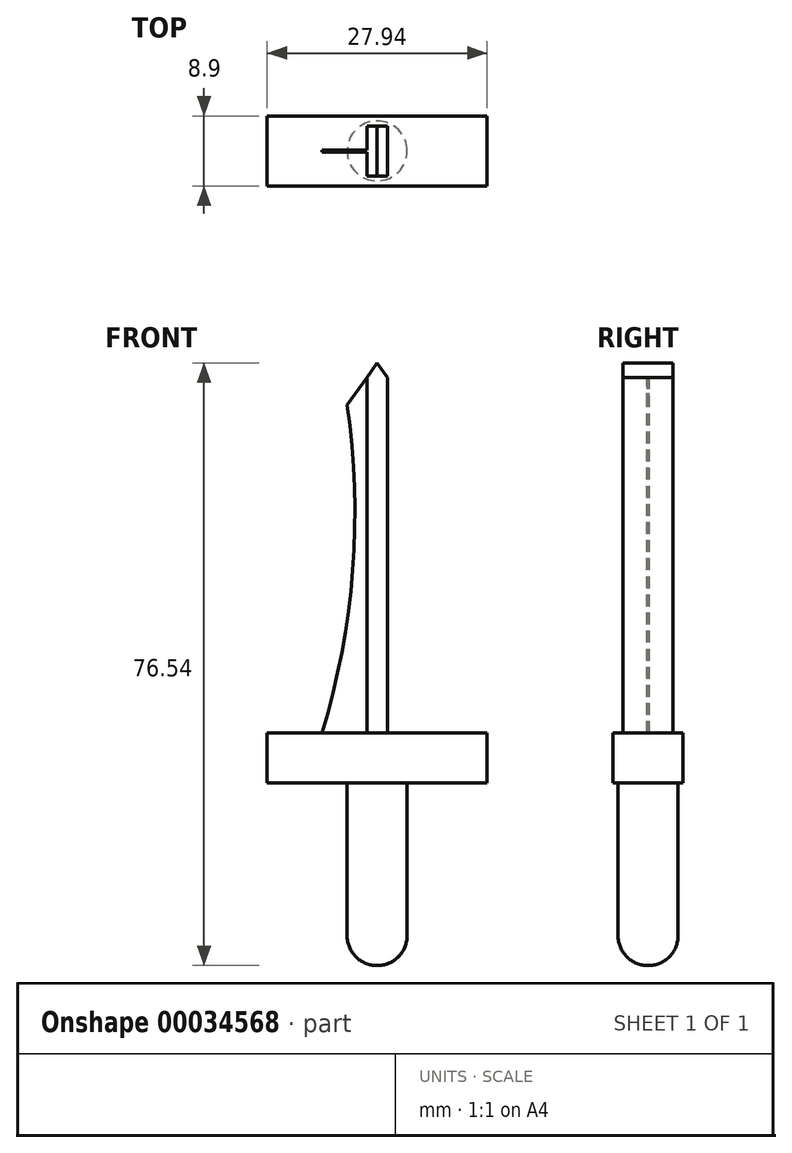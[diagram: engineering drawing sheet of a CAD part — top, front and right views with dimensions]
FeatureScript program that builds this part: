
annotation { "Feature Type Name" : "Feature", "Feature Type Description" : "" }
export const myFeature = defineFeature(function(context is Context, id is Id, definition is map)
    precondition{}
    {
        {
            var Q0;
            Q0=qCreatedBy(makeId("Front.planeOp"),FACE);
            var sketch = newSketch(context, id + "F0", { "sketchPlane" : qUnion([Q0])});
            skLineSegment(sketch, "E0.bottom", {"start": v(-34.27, 19.4) * mm, "end": v(-26.65, 19.4) * mm});
            skLineSegment(sketch, "E0.top", {"start": v(-34.27, 0.02) * mm, "end": v(-26.65, 0.02) * mm});
            skLineSegment(sketch, "E0.left", {"start": v(-34.27, 19.4) * mm, "end": v(-34.27, 0.02) * mm});
            skLineSegment(sketch, "E0.right", {"start": v(-26.65, 19.4) * mm, "end": v(-26.65, 0.02) * mm});
            skLineSegment(sketch, "E1.bottom", {"start": v(-44.43, 19.4) * mm, "end": v(-16.49, 19.4) * mm});
            skLineSegment(sketch, "E1.top", {"start": v(-44.43, 25.74) * mm, "end": v(-16.49, 25.74) * mm});
            skLineSegment(sketch, "E1.left", {"start": v(-44.43, 19.4) * mm, "end": v(-44.43, 25.74) * mm});
            skLineSegment(sketch, "E1.right", {"start": v(-16.49, 19.4) * mm, "end": v(-16.49, 25.74) * mm});
            skLineSegment(sketch, "E2", {"start": v(-34.27, 67.43) * mm, "end": v(-30.46, 72.73) * mm});
            skArc(sketch, "E3", {"start": v(-37.44, 25.74) * mm, "mid": v(-33.57, 46.41) * mm, "end": v(-34.27, 67.43) * mm});
            skLineSegment(sketch, "E4", {"start": v(-30.46, 72.73) * mm, "end": v(-30.46, 25.74) * mm});
            skArc(sketch, "E5.MirrorCS", {"start": v(-23.47, 25.74) * mm, "mid": v(-27.34, 46.41) * mm, "end": v(-26.65, 67.43) * mm});
            skLineSegment(sketch, "E6", {"start": v(-30.46, 72.73) * mm, "end": v(-26.65, 67.43) * mm});
            skPoint(sketch, "E7", {"position": v(-30.46, 19.4) * mm});
            skLineSegment(sketch, "E8", {"start": v(-30.46, 25.74) * mm, "end": v(-30.46, 19.4) * mm, "construction": true});
            skLineSegment(sketch, "E9", {"start": v(-30.46, 19.4) * mm, "end": v(-30.46, 0.02) * mm, "construction": true});
            skCircle(sketch, "E10", {"center": v(-30.46, 0) * mm, "radius": 3.81 * mm});
            skLineSegment(sketch, "E11", {"start": v(-26.65, 19.4) * mm, "end": v(-16.49, 19.4) * mm});
            skLineSegment(sketch, "E12", {"start": v(-34.27, 19.4) * mm, "end": v(-44.43, 19.4) * mm});
            skLineSegment(sketch, "E13", {"start": v(-44.43, 19.4) * mm, "end": v(-34.27, 19.4) * mm});
            skLineSegment(sketch, "E14", {"start": v(-30.46, 25.74) * mm, "end": v(-44.43, 25.74) * mm});
            skLineSegment(sketch, "E15", {"start": v(-30.46, 25.74) * mm, "end": v(-16.49, 25.74) * mm});
            skLineSegment(sketch, "E16", {"start": v(-30.46, 19.4) * mm, "end": v(-30.46, -3.81) * mm});
            skLineSegment(sketch, "E17", {"start": v(-31.76, 25.74) * mm, "end": v(-31.76, 70.92) * mm});
            skLineSegment(sketch, "E18", {"start": v(-29.15, 25.74) * mm, "end": v(-29.15, 70.92) * mm});
            skLineSegment(sketch, "E19", {"start": v(-30.46, 72.73) * mm, "end": v(-29.15, 70.92) * mm});
            skLineSegment(sketch, "E20", {"start": v(-30.46, 72.73) * mm, "end": v(-31.76, 70.92) * mm});
            skSolve(sketch);
        }
        {
            var Q0;
            {var subQ5=sQuery(id+"F0.wireOp",EDGE,"E0.right");Q0=makeQuery(id+"F0.imprint","IMPRINT",FACE,{"disambiguationData":[TD([[makeQuery(id+"F0.imprint","IMPRINT",EDGE,{"derivedFrom":subQ5}),-1.0]])]});}
            var Q1;
            {var subQ0=sQuery(id+"F0.wireOp",EDGE,"E16");var subQ3=sQuery(id+"F0.wireOp",EDGE,"E0.top");var subQ4=makeQuery(id+"F0.imprint","INTERSECT",VERTEX,{"derivedFrom":[subQ3,subQ0]});Q1=makeQuery(id+"F0.imprint","IMPRINT",FACE,{"disambiguationData":[TD([[makeQuery(id+"F0.imprint","IMPRINT",EDGE,{"disambiguationData":[TD([[subQ4,1.0]])],"derivedFrom":subQ0}),1.0]])]});}
            var Q2;
            {var subQ0=sQuery(id+"F0.wireOp",EDGE,"E16");var subQ3=sQuery(id+"F0.wireOp",EDGE,"E10");var subQ4=makeQuery(id+"F0.imprint","INTERSECT",VERTEX,{"disambiguationData":[OD(0.0)],"derivedFrom":[subQ3,subQ0]});Q2=makeQuery(id+"F0.imprint","IMPRINT",FACE,{"disambiguationData":[TD([[makeQuery(id+"F0.imprint","IMPRINT",EDGE,{"disambiguationData":[TD([[subQ4,1.0]])],"derivedFrom":subQ0}),1.0]])]});}
            var Q3;
            Q3=sQuery(id+"F0.wireOp",EDGE,"E9");
            revolve(context, id + "F1", {"entities" : qUnion([Q0, Q1, Q2]), "axis" : qUnion([Q3]), "revolveType" : RevolveType.FULL});
        }
        {
            var Q0;
            {var subQ6=sQuery(id+"F0.wireOp",EDGE,"E1.left");Q0=makeQuery(id+"F0.imprint","IMPRINT",FACE,{"disambiguationData":[TD([[makeQuery(id+"F0.imprint","IMPRINT",EDGE,{"derivedFrom":subQ6}),-1.0]])]});}
            extrude(context, id + "F2", {"entities" : qUnion([Q0]), "operationType" : NewBodyOperationType.ADD, "endBound" : BoundingType.SYMMETRIC, "depth" : 8.9 * mm});
        }
        {
            var Q0;
            {var subQ2=sQuery(id+"F0.wireOp",EDGE,"E5.MirrorCS");Q0=makeQuery(id+"F0.imprint","IMPRINT",FACE,{"disambiguationData":[TD([[makeQuery(id+"F0.imprint","IMPRINT",EDGE,{"derivedFrom":subQ2}),1.0]])]});}
            var Q1;
            Q1=makeQuery(id+"F0.imprint","IMPRINT",FACE,{"disambiguationData":[TD([[makeQuery(id+"F0.imprint","IMPRINT",EDGE,{"derivedFrom":sQuery(id+"F0.wireOp",EDGE,"E2")}),-1.0]])]});
            extrude(context, id + "F3", {"entities" : qUnion([Q0, Q1]), "operationType" : NewBodyOperationType.ADD, "endBound" : BoundingType.SYMMETRIC, "depth" : 0.25 * mm});
        }
        {
            var Q0;
            {var subQ2=sQuery(id+"F0.wireOp",EDGE,"E4");Q0=makeQuery(id+"F0.imprint","IMPRINT",FACE,{"disambiguationData":[TD([[makeQuery(id+"F0.imprint","IMPRINT",EDGE,{"derivedFrom":subQ2}),1.0]])]});}
            var Q1;
            {var subQ2=sQuery(id+"F0.wireOp",EDGE,"E4");Q1=makeQuery(id+"F0.imprint","IMPRINT",FACE,{"disambiguationData":[TD([[makeQuery(id+"F0.imprint","IMPRINT",EDGE,{"derivedFrom":subQ2}),-1.0]])]});}
            extrude(context, id + "F4", {"entities" : qUnion([Q0, Q1]), "operationType" : NewBodyOperationType.ADD, "endBound" : BoundingType.SYMMETRIC, "depth" : 6.35 * mm});
        }
    });
